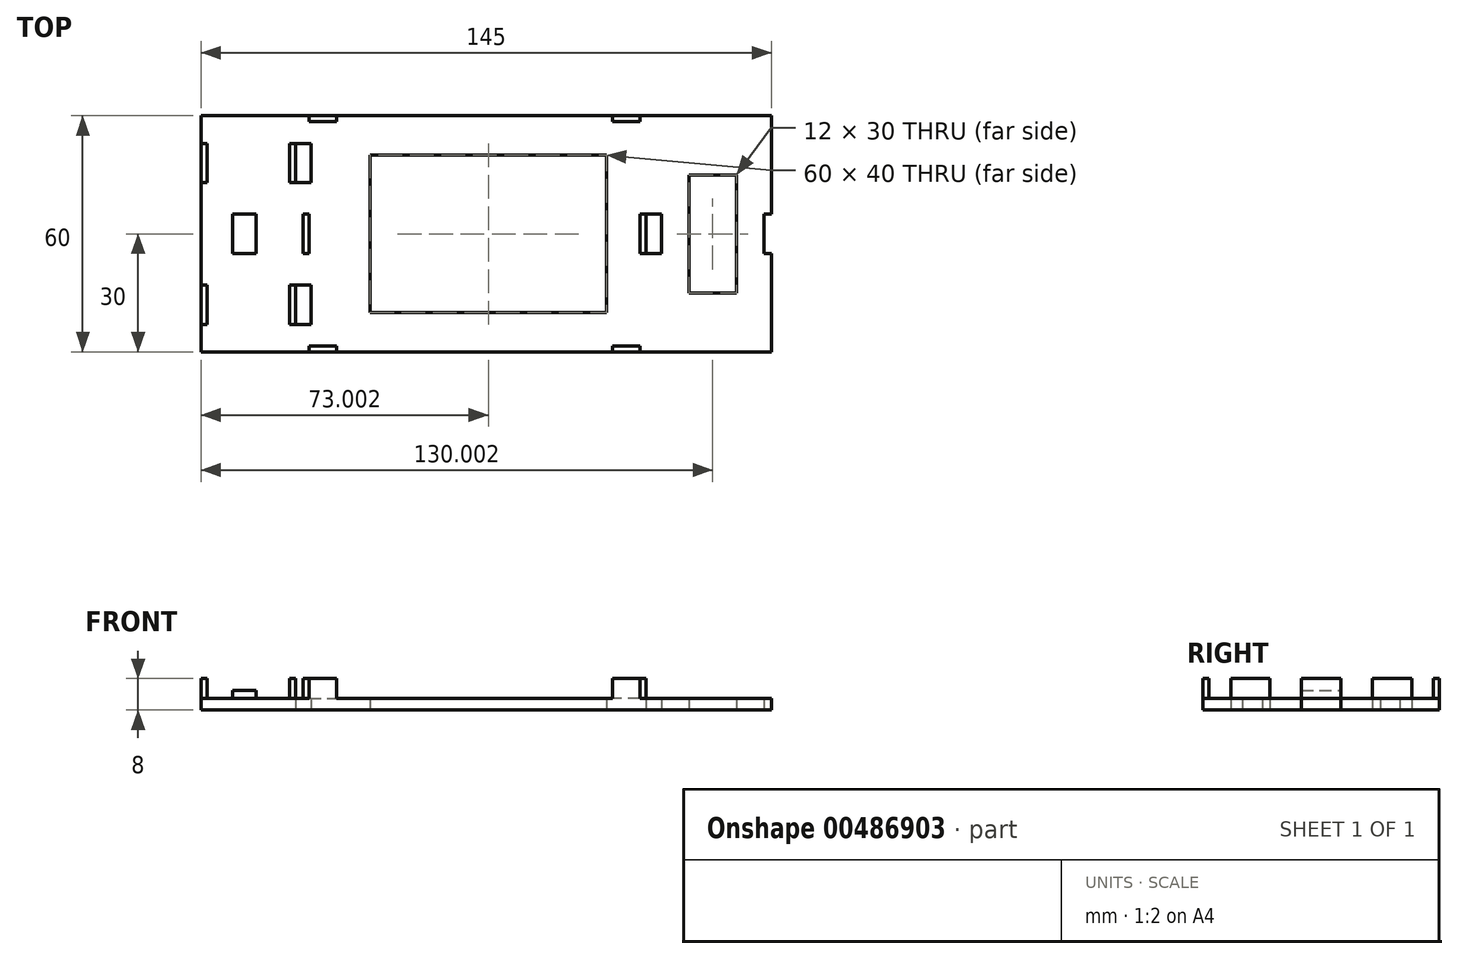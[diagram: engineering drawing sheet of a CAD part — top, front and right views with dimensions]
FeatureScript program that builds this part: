
annotation { "Feature Type Name" : "Feature", "Feature Type Description" : "" }
export const myFeature = defineFeature(function(context is Context, id is Id, definition is map)
    precondition{}
    {
        {
            var Q0;
            Q0=qCreatedBy(makeId("Top.planeOp"),FACE);
            var sketch = newSketch(context, id + "F0", { "sketchPlane" : qUnion([Q0])});
            skLineSegment(sketch, "E0.bottom", {"start": v(-90.65, 30) * mm, "end": v(54.35, 30) * mm});
            skLineSegment(sketch, "E0.top", {"start": v(-90.65, -30) * mm, "end": v(54.35, -30) * mm});
            skLineSegment(sketch, "E0.left", {"start": v(-90.65, 30) * mm, "end": v(-90.65, -30) * mm});
            skLineSegment(sketch, "E0.right", {"start": v(54.35, 30) * mm, "end": v(54.35, 5) * mm});
            skLineSegment(sketch, "E1", {"start": v(-90.65, 0) * mm, "end": v(107.34, 0) * mm, "construction": true});
            skLineSegment(sketch, "E2.bottom", {"start": v(-66.65, -23) * mm, "end": v(-62.65, -23) * mm});
            skLineSegment(sketch, "E2.top", {"start": v(-66.65, -13) * mm, "end": v(-62.65, -13) * mm});
            skLineSegment(sketch, "E2.left", {"start": v(-66.65, -23) * mm, "end": v(-66.65, -13) * mm});
            skLineSegment(sketch, "E2.right", {"start": v(-62.65, -23) * mm, "end": v(-62.65, -13) * mm});
            skLineSegment(sketch, "E3.MirrorCS", {"start": v(-66.65, 23) * mm, "end": v(-62.65, 23) * mm});
            skLineSegment(sketch, "E4.MirrorCS", {"start": v(-66.65, 13) * mm, "end": v(-62.65, 13) * mm});
            skLineSegment(sketch, "E5.MirrorCS", {"start": v(-62.65, 23) * mm, "end": v(-62.65, 13) * mm});
            skLineSegment(sketch, "E6.MirrorCS", {"start": v(-66.65, 23) * mm, "end": v(-66.65, 13) * mm});
            skLineSegment(sketch, "E7.bottom", {"start": v(-47.65, -20) * mm, "end": v(12.35, -20) * mm});
            skLineSegment(sketch, "E7.top", {"start": v(-47.65, 20) * mm, "end": v(12.35, 20) * mm});
            skLineSegment(sketch, "E7.left", {"start": v(-47.65, -20) * mm, "end": v(-47.65, 20) * mm});
            skLineSegment(sketch, "E7.right", {"start": v(12.35, -20) * mm, "end": v(12.35, 20) * mm});
            skLineSegment(sketch, "E8.bottom", {"start": v(22.35, -5) * mm, "end": v(26.35, -5) * mm});
            skLineSegment(sketch, "E8.top", {"start": v(22.35, 5) * mm, "end": v(26.35, 5) * mm});
            skLineSegment(sketch, "E8.left", {"start": v(22.35, -5) * mm, "end": v(22.35, 5) * mm});
            skLineSegment(sketch, "E8.right", {"start": v(26.35, -5) * mm, "end": v(26.35, 5) * mm});
            skLineSegment(sketch, "E9.bottom", {"start": v(45.35, -15) * mm, "end": v(33.35, -15) * mm});
            skLineSegment(sketch, "E9.top", {"start": v(45.35, 15) * mm, "end": v(33.35, 15) * mm});
            skLineSegment(sketch, "E9.left", {"start": v(45.35, -15) * mm, "end": v(45.35, 15) * mm});
            skLineSegment(sketch, "E9.right", {"start": v(33.35, -15) * mm, "end": v(33.35, 15) * mm});
            skLineSegment(sketch, "E10.bottom", {"start": v(54.35, -5) * mm, "end": v(52.35, -5) * mm});
            skLineSegment(sketch, "E10.top", {"start": v(54.35, 5) * mm, "end": v(52.35, 5) * mm});
            skLineSegment(sketch, "E10.right", {"start": v(52.35, -5) * mm, "end": v(52.35, 5) * mm});
            skLineSegment(sketch, "E11.trimOffspring", {"start": v(54.35, -5) * mm, "end": v(54.35, -30) * mm});
            skSolve(sketch);
        }
        {
            var Q0;
            Q0=makeQuery(id+"F0.imprint","IMPRINT",FACE,{"disambiguationData":[TD([[makeQuery(id+"F0.imprint","IMPRINT",EDGE,{"derivedFrom":sQuery(id+"F0.wireOp",EDGE,"E0.top")}),1.0]])]});
            extrude(context, id + "F1", {"entities" : qUnion([Q0]), "depth" : 3 * mm, "offsetDistance" : 25 * mm});
        }
        {
            var Q0;
            Q0=makeQuery(id+"F1.opExtrude","CAP_FACE",FACE,{"disambiguationData":[OSD([sQuery(id+"F0.wireOp",EDGE,"E0.top"),sQuery(id+"F0.wireOp",EDGE,"E0.left"),sQuery(id+"F0.wireOp",EDGE,"E0.right"),sQuery(id+"F0.wireOp",EDGE,"E2.bottom"),sQuery(id+"F0.wireOp",EDGE,"E2.top"),sQuery(id+"F0.wireOp",EDGE,"E2.left"),sQuery(id+"F0.wireOp",EDGE,"E2.right"),sQuery(id+"F0.wireOp",EDGE,"E3.MirrorCS"),sQuery(id+"F0.wireOp",EDGE,"E4.MirrorCS"),sQuery(id+"F0.wireOp",EDGE,"E5.MirrorCS"),sQuery(id+"F0.wireOp",EDGE,"E0.bottom"),sQuery(id+"F0.wireOp",EDGE,"E6.MirrorCS"),sQuery(id+"F0.wireOp",EDGE,"E7.bottom"),sQuery(id+"F0.wireOp",EDGE,"E7.top"),sQuery(id+"F0.wireOp",EDGE,"E7.left"),sQuery(id+"F0.wireOp",EDGE,"E7.right"),sQuery(id+"F0.wireOp",EDGE,"E8.bottom"),sQuery(id+"F0.wireOp",EDGE,"E8.top"),sQuery(id+"F0.wireOp",EDGE,"E8.left"),sQuery(id+"F0.wireOp",EDGE,"E8.right")])],"isStart":false});
            var sketch = newSketch(context, id + "F2", { "sketchPlane" : qUnion([Q0])});
            skLineSegment(sketch, "E12.bottom", {"start": v(-66.65, -13) * mm, "end": v(-68.15, -13) * mm});
            skLineSegment(sketch, "E12.top", {"start": v(-66.65, -23) * mm, "end": v(-68.15, -23) * mm});
            skLineSegment(sketch, "E12.left", {"start": v(-66.65, -13) * mm, "end": v(-66.65, -23) * mm});
            skLineSegment(sketch, "E12.right", {"start": v(-68.15, -13) * mm, "end": v(-68.15, -23) * mm});
            skLineSegment(sketch, "E13.bottom", {"start": v(-90.65, -13) * mm, "end": v(-89.15, -13) * mm});
            skLineSegment(sketch, "E13.top", {"start": v(-90.65, -23) * mm, "end": v(-89.15, -23) * mm});
            skLineSegment(sketch, "E13.left", {"start": v(-90.65, -13) * mm, "end": v(-90.65, -23) * mm});
            skLineSegment(sketch, "E13.right", {"start": v(-89.15, -13) * mm, "end": v(-89.15, -23) * mm});
            skLineSegment(sketch, "E14.bottom", {"start": v(-66.65, 13) * mm, "end": v(-68.15, 13) * mm});
            skLineSegment(sketch, "E14.top", {"start": v(-66.65, 23) * mm, "end": v(-68.15, 23) * mm});
            skLineSegment(sketch, "E14.left", {"start": v(-66.65, 13) * mm, "end": v(-66.65, 23) * mm});
            skLineSegment(sketch, "E14.right", {"start": v(-68.15, 13) * mm, "end": v(-68.15, 23) * mm});
            skLineSegment(sketch, "E15.bottom", {"start": v(-90.65, 23) * mm, "end": v(-89.15, 23) * mm});
            skLineSegment(sketch, "E15.top", {"start": v(-90.65, 13) * mm, "end": v(-89.15, 13) * mm});
            skLineSegment(sketch, "E15.left", {"start": v(-90.65, 23) * mm, "end": v(-90.65, 13) * mm});
            skLineSegment(sketch, "E15.right", {"start": v(-89.15, 23) * mm, "end": v(-89.15, 13) * mm});
            skLineSegment(sketch, "E16.bottom", {"start": v(-63.15, -30) * mm, "end": v(-56.15, -30) * mm});
            skLineSegment(sketch, "E16.top", {"start": v(-63.15, -28.5) * mm, "end": v(-56.15, -28.5) * mm});
            skLineSegment(sketch, "E16.left", {"start": v(-63.15, -30) * mm, "end": v(-63.15, -28.5) * mm});
            skLineSegment(sketch, "E16.right", {"start": v(-56.15, -30) * mm, "end": v(-56.15, -28.5) * mm});
            skLineSegment(sketch, "E17.bottom", {"start": v(20.85, -30) * mm, "end": v(13.85, -30) * mm});
            skLineSegment(sketch, "E17.top", {"start": v(20.85, -28.5) * mm, "end": v(13.85, -28.5) * mm});
            skLineSegment(sketch, "E17.left", {"start": v(20.85, -30) * mm, "end": v(20.85, -28.5) * mm});
            skLineSegment(sketch, "E17.right", {"start": v(13.85, -30) * mm, "end": v(13.85, -28.5) * mm});
            skLineSegment(sketch, "E18.bottom", {"start": v(-63.15, 30) * mm, "end": v(-56.15, 30) * mm});
            skLineSegment(sketch, "E18.top", {"start": v(-63.15, 28.5) * mm, "end": v(-56.15, 28.5) * mm});
            skLineSegment(sketch, "E18.left", {"start": v(-63.15, 30) * mm, "end": v(-63.15, 28.5) * mm});
            skLineSegment(sketch, "E18.right", {"start": v(-56.15, 30) * mm, "end": v(-56.15, 28.5) * mm});
            skLineSegment(sketch, "E19.bottom", {"start": v(20.85, 30) * mm, "end": v(13.85, 30) * mm});
            skLineSegment(sketch, "E19.top", {"start": v(20.85, 28.5) * mm, "end": v(13.85, 28.5) * mm});
            skLineSegment(sketch, "E19.left", {"start": v(20.85, 30) * mm, "end": v(20.85, 28.5) * mm});
            skLineSegment(sketch, "E19.right", {"start": v(13.85, 30) * mm, "end": v(13.85, 28.5) * mm});
            skLineSegment(sketch, "E20.bottom", {"start": v(22.35, 5) * mm, "end": v(20.85, 5) * mm});
            skLineSegment(sketch, "E20.top", {"start": v(22.35, -5) * mm, "end": v(20.85, -5) * mm});
            skLineSegment(sketch, "E20.left", {"start": v(22.35, 5) * mm, "end": v(22.35, -5) * mm});
            skLineSegment(sketch, "E20.right", {"start": v(20.85, 5) * mm, "end": v(20.85, -5) * mm});
            skLineSegment(sketch, "E21.bottom", {"start": v(-63.15, -5) * mm, "end": v(-64.65, -5) * mm});
            skLineSegment(sketch, "E21.top", {"start": v(-63.15, 5) * mm, "end": v(-64.65, 5) * mm});
            skLineSegment(sketch, "E21.left", {"start": v(-63.15, -5) * mm, "end": v(-63.15, 5) * mm});
            skLineSegment(sketch, "E21.right", {"start": v(-64.65, -5) * mm, "end": v(-64.65, 5) * mm});
            skSolve(sketch);
        }
        {
            var Q0;
            Q0 = qSketchRegion(id + "F2", true);
            extrude(context, id + "F3", {"entities" : qUnion([Q0]), "operationType" : NewBodyOperationType.ADD, "depth" : 5 * mm, "offsetDistance" : 25 * mm});
        }
        {
            var Q0;
            Q0=makeQuery(id+"F1.opExtrude","CAP_FACE",FACE,{"disambiguationData":[OSD([sQuery(id+"F0.wireOp",EDGE,"E0.top"),sQuery(id+"F0.wireOp",EDGE,"E0.left"),sQuery(id+"F0.wireOp",EDGE,"E0.right"),sQuery(id+"F0.wireOp",EDGE,"E2.bottom"),sQuery(id+"F0.wireOp",EDGE,"E2.top"),sQuery(id+"F0.wireOp",EDGE,"E2.left"),sQuery(id+"F0.wireOp",EDGE,"E2.right"),sQuery(id+"F0.wireOp",EDGE,"E3.MirrorCS"),sQuery(id+"F0.wireOp",EDGE,"E4.MirrorCS"),sQuery(id+"F0.wireOp",EDGE,"E5.MirrorCS"),sQuery(id+"F0.wireOp",EDGE,"E0.bottom"),sQuery(id+"F0.wireOp",EDGE,"E6.MirrorCS"),sQuery(id+"F0.wireOp",EDGE,"E7.bottom"),sQuery(id+"F0.wireOp",EDGE,"E7.top"),sQuery(id+"F0.wireOp",EDGE,"E7.left"),sQuery(id+"F0.wireOp",EDGE,"E7.right"),sQuery(id+"F0.wireOp",EDGE,"E8.bottom"),sQuery(id+"F0.wireOp",EDGE,"E8.top"),sQuery(id+"F0.wireOp",EDGE,"E8.left"),sQuery(id+"F0.wireOp",EDGE,"E8.right")])],"isStart":false});
            var sketch = newSketch(context, id + "F4", { "sketchPlane" : qUnion([Q0])});
            skLineSegment(sketch, "E22.bottom", {"start": v(-76.65, -5) * mm, "end": v(-82.65, -5) * mm});
            skLineSegment(sketch, "E22.top", {"start": v(-76.65, 5) * mm, "end": v(-82.65, 5) * mm});
            skLineSegment(sketch, "E22.left", {"start": v(-76.65, -5) * mm, "end": v(-76.65, 5) * mm});
            skLineSegment(sketch, "E22.right", {"start": v(-82.65, -5) * mm, "end": v(-82.65, 5) * mm});
            skSolve(sketch);
        }
        {
            var Q0;
            Q0=makeQuery(id+"F4.imprint","IMPRINT",FACE,{"disambiguationData":[TD([[makeQuery(id+"F4.imprint","IMPRINT",EDGE,{"derivedFrom":sQuery(id+"F4.wireOp",EDGE,"E22.bottom")}),-1.0]])]});
            extrude(context, id + "F5", {"entities" : qUnion([Q0]), "operationType" : NewBodyOperationType.ADD, "depth" : 2 * mm, "offsetDistance" : 25 * mm});
        }
    });
